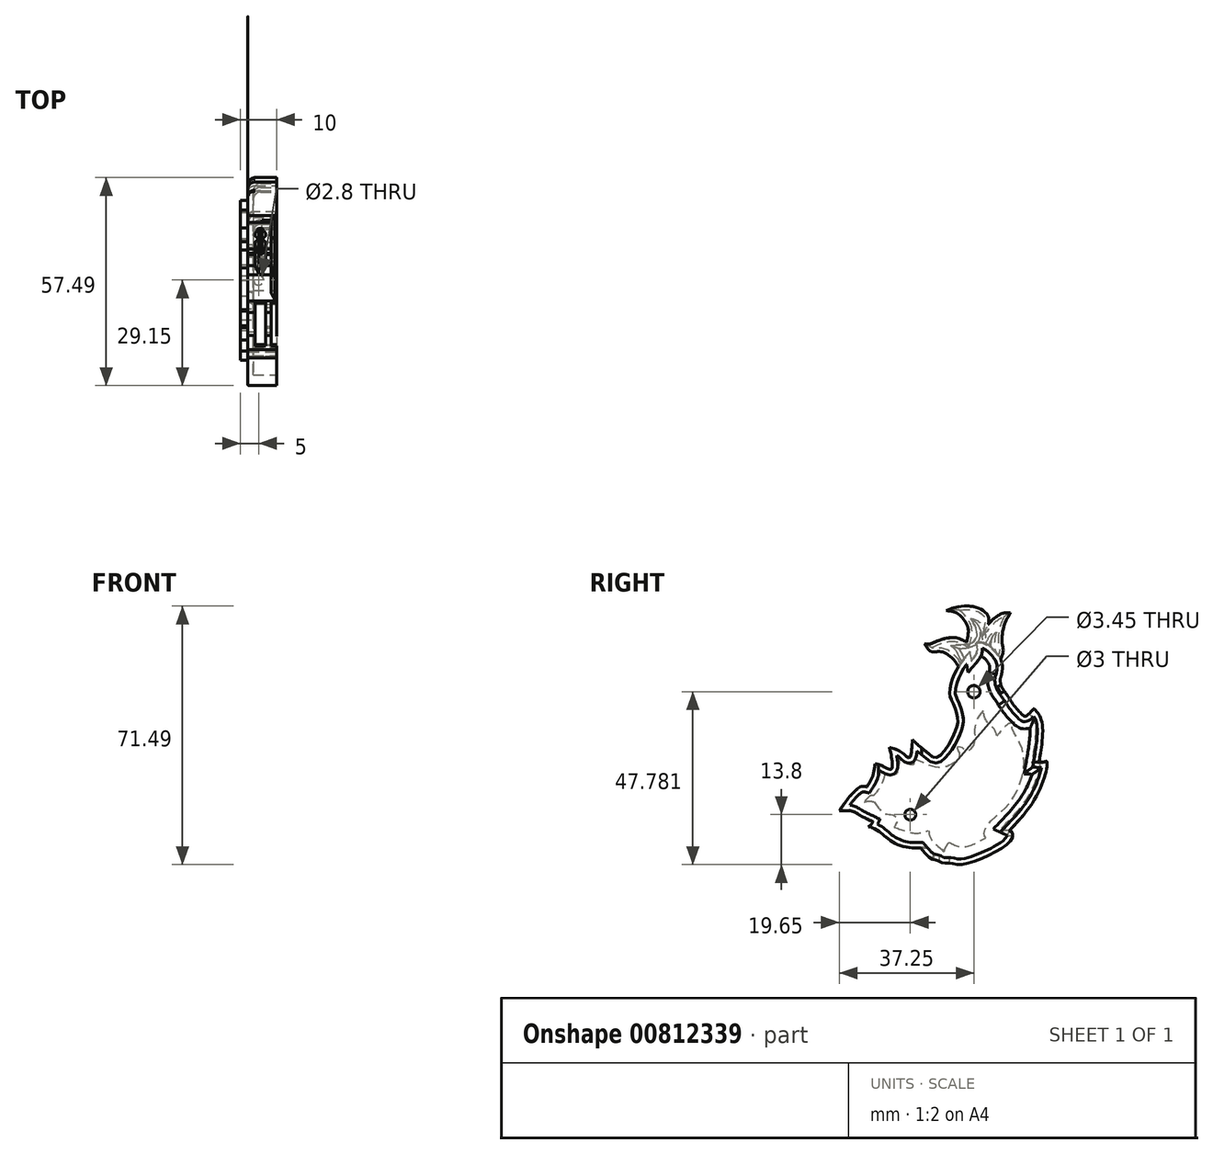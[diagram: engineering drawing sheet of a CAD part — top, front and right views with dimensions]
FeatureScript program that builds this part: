
annotation { "Feature Type Name" : "Feature", "Feature Type Description" : "" }
export const myFeature = defineFeature(function(context is Context, id is Id, definition is map)
    precondition{}
    {
        {
            var Q0;
            Q0=qCreatedBy(makeId("Right.planeOp"),FACE);
            var sketch = newSketch(context, id + "F0", { "sketchPlane" : qUnion([Q0])});
            skPoint(sketch, "E0", {"position": v(40.6, 0) * mm});
            skPoint(sketch, "E1", {"position": v(0, -40.6) * mm});
            skSolve(sketch);
        }
        {
            var Q0;
            Q0=qCreatedBy(makeId("Right.planeOp"),FACE);
            var sketch = newSketch(context, id + "F1", { "sketchPlane" : qUnion([Q0])});
            skFitSpline(sketch, "E2", {"points": [v(-3.24, 0) * mm, v(0.5, -2.14) * mm, v(5.33, 4.74) * mm, v(6.1, 8.94) * mm, v(4.7, 13.13) * mm, v(3.93, 15.55) * mm, v(4.82, 19.88) * mm, v(6.47, 23.19) * mm], "startDerivative": vector(37.62, -30.46) * mm, "endDerivative": vector(13.33, 23.15) * mm});
            skFitSpline(sketch, "E3", {"points": [v(6.47, 23.19) * mm, v(7.57, 24.79) * mm, v(9.54, 27.14) * mm], "startDerivative": vector(2.25, 3.48) * mm, "endDerivative": vector(3.82, 4.4) * mm});
            skFitSpline(sketch, "E4", {"points": [v(9.54, 27.14) * mm, v(9.93, 24.79) * mm], "startDerivative": vector(0.4, -2.35) * mm, "endDerivative": vector(0.4, -2.35) * mm});
            skFitSpline(sketch, "E5", {"points": [v(9.93, 24.79) * mm, v(11.4, 27.14) * mm, v(11.1, 29.4) * mm], "startDerivative": vector(3.7, 4.42) * mm, "endDerivative": vector(-1.43, 4.81) * mm});
            skFitSpline(sketch, "E6", {"points": [v(11.1, 29.4) * mm, v(11.78, 29.7) * mm, v(12.83, 29.7) * mm, v(15.34, 28.3) * mm, v(18.25, 24.34) * mm, v(18.14, 20.25) * mm], "startDerivative": vector(5.83, 3.18) * mm, "endDerivative": vector(-3.05, -15.82) * mm});
            skFitSpline(sketch, "E7", {"points": [v(20.33, 14.28) * mm, v(23.93, 9.7) * mm, v(24.82, 9.24) * mm, v(27.16, 11.36) * mm], "startDerivative": vector(7.36, -13.07) * mm, "endDerivative": vector(7.66, 8.58) * mm});
            skFitSpline(sketch, "E8", {"points": [v(27.16, 11.36) * mm, v(28.52, 9.77) * mm, v(29.58, 6.07) * mm, v(28.98, -1.2) * mm, v(28.6, -3.47) * mm], "startDerivative": vector(7.57, -7.48) * mm, "endDerivative": vector(-1.64, -9.32) * mm});
            skFitSpline(sketch, "E9", {"points": [v(28.6, -3.47) * mm, v(29.59, -3.47) * mm, v(30.76, -3.19) * mm], "startDerivative": vector(2.05, -0.13) * mm, "endDerivative": vector(2.26, 0.67) * mm});
            skFitSpline(sketch, "E10", {"points": [v(30.76, -3.19) * mm, v(30.76, -5.2) * mm, v(27.33, -13.82) * mm, v(20.4, -22.38) * mm], "startDerivative": vector(1.2, -9.04) * mm, "endDerivative": vector(-17.5, -18.45) * mm});
            skFitSpline(sketch, "E11", {"points": [v(20.4, -22.38) * mm, v(21.13, -22.88) * mm, v(21.29, -24.17) * mm, v(19.32, -26.59) * mm, v(12.59, -30.14) * mm, v(6.69, -31.8) * mm, v(4.01, -31.38) * mm, v(2.05, -31.37) * mm, v(0.26, -30.52) * mm, v(-0.96, -30.31) * mm, v(-4.15, -27.22) * mm], "startDerivative": vector(14.78, -6.8) * mm, "endDerivative": vector(-27.99, 32.68) * mm});
            skFitSpline(sketch, "E12", {"points": [v(-4.15, -27.22) * mm, v(-8.6, -26.89) * mm, v(-12.79, -24.96) * mm, v(-15.21, -22.93) * mm, v(-17.91, -21.45) * mm, v(-18.54, -21.31) * mm], "startDerivative": vector(-18.02, -0.18) * mm, "endDerivative": vector(-5.5, 0.56) * mm});
            skFitSpline(sketch, "E13", {"points": [v(-18.54, -21.31) * mm, v(-17.72, -20.58) * mm, v(-17.36, -19.97) * mm], "startDerivative": vector(1.69, 1.29) * mm, "endDerivative": vector(0.63, 1.4) * mm});
            skPoint(sketch, "E14.end.orphan", {"position": v(-24.75, -14.2) * mm});
            skFitSpline(sketch, "E15", {"points": [v(-17.36, -19.97) * mm, v(-21.03, -18.12) * mm, v(-23.14, -17.03) * mm, v(-26.65, -16.95) * mm], "startDerivative": vector(-10.75, 5.04) * mm, "endDerivative": vector(-11.13, -0.75) * mm});
            skFitSpline(sketch, "E16", {"points": [v(-26.65, -16.95) * mm, v(-23.68, -12.9) * mm, v(-20.64, -10.25) * mm, v(-19, -10.33) * mm], "startDerivative": vector(6.9, 10.1) * mm, "endDerivative": vector(6.75, -1.8) * mm});
            skFitSpline(sketch, "E17", {"points": [v(-19, -10.33) * mm, v(-17.46, -7.5) * mm, v(-16.72, -3.96) * mm], "startDerivative": vector(3.61, 5.56) * mm, "endDerivative": vector(0.98, 7.15) * mm});
            skFitSpline(sketch, "E18", {"points": [v(-16.72, -3.96) * mm, v(-14.8, -4.47) * mm, v(-12.27, -5.38) * mm, v(-12.38, -1.03) * mm, v(-12.78, 0.59) * mm], "startDerivative": vector(7.9, -0.88) * mm, "endDerivative": vector(-1.71, 5.84) * mm});
            skFitSpline(sketch, "E19", {"points": [v(-12.78, 0.59) * mm, v(-9.24, -0.83) * mm, v(-7.22, -2.24) * mm, v(-6.43, 2.8) * mm], "startDerivative": vector(10.6, -2.72) * mm, "endDerivative": vector(0.94, 15.88) * mm});
            skFitSpline(sketch, "E20", {"points": [v(-6.43, 2.8) * mm, v(-4.74, 1.17) * mm, v(-3.24, 0) * mm], "startDerivative": vector(3.21, -3.25) * mm, "endDerivative": vector(3.16, -2.33) * mm});
            skFitSpline(sketch, "E21", {"points": [v(20.33, 14.28) * mm, v(19.55, 15.4) * mm, v(18.07, 17.87) * mm, v(18.14, 20.25) * mm], "startDerivative": vector(-3.19, 3.99) * mm, "endDerivative": vector(2.56, 3.4) * mm});
            skSolve(sketch);
        }
        {
            var Q0;
            Q0 = qSketchRegion(id + "F1", true);
            extrude(context, id + "F2", {"entities" : qUnion([Q0]), "oppositeDirection" : true, "depth" : 8 * mm, "offsetDistance" : 25 * mm});
        }
        {
            var Q0;
            Q0=qCreatedBy(makeId("Right.planeOp"),FACE);
            var sketch = newSketch(context, id + "F3", { "sketchPlane" : qUnion([Q0])});
            skCircle(sketch, "E22", {"center": v(10.6, 15.98) * mm, "radius": 1.73 * mm});
            skSolve(sketch);
        }
        {
            var Q0;
            Q0=makeQuery(id+"F2.opExtrude","CAP_FACE",FACE,{"disambiguationData":[OSD([sQuery(id+"F1.wireOp",EDGE,"E2"),sQuery(id+"F1.wireOp",EDGE,"E3"),sQuery(id+"F1.wireOp",EDGE,"E4"),sQuery(id+"F1.wireOp",EDGE,"E5"),sQuery(id+"F1.wireOp",EDGE,"E6"),sQuery(id+"F1.wireOp",EDGE,"b648baaf-3003-42c2-b2da-362ff8d469fc"),sQuery(id+"F1.wireOp",EDGE,"f09f861e-65dd-4840-b0a7-49bf3a0d17f7"),sQuery(id+"F1.wireOp",EDGE,"9c976f9a-3d35-419b-9c2e-039097bb7361"),sQuery(id+"F1.wireOp",EDGE,"E7"),sQuery(id+"F1.wireOp",EDGE,"E8"),sQuery(id+"F1.wireOp",EDGE,"E9"),sQuery(id+"F1.wireOp",EDGE,"E10"),sQuery(id+"F1.wireOp",EDGE,"E11"),sQuery(id+"F1.wireOp",EDGE,"E12"),sQuery(id+"F1.wireOp",EDGE,"E13"),sQuery(id+"F1.wireOp",EDGE,"E15"),sQuery(id+"F1.wireOp",EDGE,"E16"),sQuery(id+"F1.wireOp",EDGE,"E17"),sQuery(id+"F1.wireOp",EDGE,"E18"),sQuery(id+"F1.wireOp",EDGE,"E19"),sQuery(id+"F1.wireOp",EDGE,"E20")])],"isStart":true});
            shell(context, id + "F4", {"entities" : qUnion([Q0]), "thickness" : 1.5 * mm});
        }
        {
            var Q0;
            Q0 = qSketchRegion(id + "F3", true);
            extrude(context, id + "F5", {"entities" : qUnion([Q0]), "operationType" : NewBodyOperationType.REMOVE, "oppositeDirection" : true, "depth" : 25 * mm, "offsetDistance" : 25 * mm});
        }
        {
            var Q0;
            Q0=makeQuery(id+"F2.opExtrude","CAP_FACE",FACE,{"disambiguationData":[OSD([sQuery(id+"F1.wireOp",EDGE,"E2"),sQuery(id+"F1.wireOp",EDGE,"E3"),sQuery(id+"F1.wireOp",EDGE,"E4"),sQuery(id+"F1.wireOp",EDGE,"E5"),sQuery(id+"F1.wireOp",EDGE,"E6"),sQuery(id+"F1.wireOp",EDGE,"b648baaf-3003-42c2-b2da-362ff8d469fc"),sQuery(id+"F1.wireOp",EDGE,"f09f861e-65dd-4840-b0a7-49bf3a0d17f7"),sQuery(id+"F1.wireOp",EDGE,"9c976f9a-3d35-419b-9c2e-039097bb7361"),sQuery(id+"F1.wireOp",EDGE,"E7"),sQuery(id+"F1.wireOp",EDGE,"E8"),sQuery(id+"F1.wireOp",EDGE,"E9"),sQuery(id+"F1.wireOp",EDGE,"E10"),sQuery(id+"F1.wireOp",EDGE,"E11"),sQuery(id+"F1.wireOp",EDGE,"E12"),sQuery(id+"F1.wireOp",EDGE,"E13"),sQuery(id+"F1.wireOp",EDGE,"E15"),sQuery(id+"F1.wireOp",EDGE,"E16"),sQuery(id+"F1.wireOp",EDGE,"E17"),sQuery(id+"F1.wireOp",EDGE,"E18"),sQuery(id+"F1.wireOp",EDGE,"E19"),sQuery(id+"F1.wireOp",EDGE,"E20")])],"isStart":false});
            var sketch = newSketch(context, id + "F6", { "sketchPlane" : qUnion([Q0])});
            skFitSpline(sketch, "E23", {"points": [v(-16.94, 3.72) * mm, v(-16.28, 5.54) * mm, v(-14.13, 7.85) * mm, v(-13.14, 10.82) * mm], "startDerivative": vector(1.3, 6.56) * mm, "endDerivative": vector(1.63, 8.78) * mm});
            skFitSpline(sketch, "E24", {"points": [v(-13.14, 10.82) * mm, v(-11, 7.19) * mm, v(-10.83, 3.06) * mm, v(-10.34, 1.08) * mm, v(-8.63, -0.5) * mm, v(-7.42, 0.48) * mm, v(-5.9, 0.63) * mm], "startDerivative": vector(12.48, -15.59) * mm, "endDerivative": vector(12.54, -1.6) * mm});
            skFitSpline(sketch, "E25", {"points": [v(-5.9, 0.63) * mm, v(-6.36, -0.5) * mm, v(-6.5, -2.1) * mm, v(-4.54, -3.99) * mm, v(-0.91, -4.97) * mm, v(5.75, -2.55) * mm], "startDerivative": vector(-3.58, -8.34) * mm, "endDerivative": vector(23, 11.15) * mm});
            skFitSpline(sketch, "E26", {"points": [v(5.75, -2.55) * mm, v(6.02, -3.35) * mm, v(5.94, -4.12) * mm], "startDerivative": vector(0.72, -1.57) * mm, "endDerivative": vector(-0.34, -1.59) * mm});
            skFitSpline(sketch, "E27", {"points": [v(5.94, -4.12) * mm, v(7.2, -4.12) * mm, v(9.02, -2.97) * mm, v(10.18, -1.51) * mm], "startDerivative": vector(4.26, -0.66) * mm, "endDerivative": vector(2.95, 4.28) * mm});
            skFitSpline(sketch, "E28", {"points": [v(10.18, -1.51) * mm, v(10.03, -3.22) * mm, v(10.7, -6.67) * mm], "startDerivative": vector(-0.7, -3.8) * mm, "endDerivative": vector(1.58, -6.36) * mm});
            skFitSpline(sketch, "E29", {"points": [v(10.7, -6.67) * mm, v(11.92, -7.06) * mm, v(14.12, -6.34) * mm], "startDerivative": vector(2.66, -1.38) * mm, "endDerivative": vector(4.12, 1.88) * mm});
            skFitSpline(sketch, "E30", {"points": [v(14.12, -6.34) * mm, v(14.57, -8.77) * mm, v(16.73, -12.28) * mm, v(17.18, -12.77) * mm], "startDerivative": vector(0.23, -6.2) * mm, "endDerivative": vector(1.91, -1.84) * mm});
            skFitSpline(sketch, "E31", {"points": [v(17.18, -12.77) * mm, v(18, -12.77) * mm, v(19.7, -14.48) * mm], "startDerivative": vector(2.13, 0.5) * mm, "endDerivative": vector(2.86, -3.54) * mm});
            skFitSpline(sketch, "E32", {"points": [v(19.7, -14.48) * mm, v(18.4, -14.25) * mm, v(16.95, -14.48) * mm], "startDerivative": vector(-2.64, 0.68) * mm, "endDerivative": vector(-2.86, -0.67) * mm});
            skFitSpline(sketch, "E33", {"points": [v(16.95, -14.48) * mm, v(15.69, -16.27) * mm, v(14.12, -17.67) * mm, v(11.9, -18.08) * mm, v(10.7, -19.01) * mm, v(10.9, -20.53) * mm, v(11.43, -21.46) * mm], "startDerivative": vector(-6.56, -9.7) * mm, "endDerivative": vector(4.17, -6.37) * mm});
            skFitSpline(sketch, "E34", {"points": [v(11.43, -21.46) * mm, v(7.7, -22.72) * mm, v(4.92, -23.12) * mm, v(1.9, -22.38) * mm], "startDerivative": vector(-10.55, -3.79) * mm, "endDerivative": vector(-9.42, 3.13) * mm});
            skFitSpline(sketch, "E35", {"points": [v(1.9, -22.38) * mm, v(1.33, -24.66) * mm, v(-2.36, -28.17) * mm], "startDerivative": vector(-0.45, -5.6) * mm, "endDerivative": vector(-7.62, -5.97) * mm});
            skFitSpline(sketch, "E36", {"points": [v(-2.36, -28.17) * mm, v(-2.8, -27) * mm, v(-3.7, -25.65) * mm], "startDerivative": vector(-0.8, 2.5) * mm, "endDerivative": vector(-1.88, 2.55) * mm});
            skFitSpline(sketch, "E37", {"points": [v(-3.7, -25.65) * mm, v(-6.46, -26.79) * mm, v(-9.3, -26.6) * mm, v(-13.93, -24.36) * mm], "startDerivative": vector(-9.04, -4.62) * mm, "endDerivative": vector(-12.18, 6.83) * mm});
            skFitSpline(sketch, "E38", {"points": [v(-13.93, -24.36) * mm, v(-13.5, -23.75) * mm, v(-13.5, -22.38) * mm, v(-15.76, -19.24) * mm, v(-19.88, -15.51) * mm, v(-23.5, -8.94) * mm, v(-24.41, -2.03) * mm, v(-22.5, 3.31) * mm, v(-21.1, 6.11) * mm, v(-21.87, 7.51) * mm], "startDerivative": vector(9.7, 10.6) * mm, "endDerivative": vector(-15.5, 17.7) * mm});
            skFitSpline(sketch, "E39", {"points": [v(-21.87, 7.51) * mm, v(-20.07, 7.05) * mm, v(-16.94, 3.72) * mm], "startDerivative": vector(4.52, -0.37) * mm, "endDerivative": vector(5.28, -6.74) * mm});
            skSolve(sketch);
        }
        {
            var Q0;
            Q0 = qSketchRegion(id + "F6", true);
            extrude(context, id + "F7", {"entities" : qUnion([Q0]), "operationType" : NewBodyOperationType.ADD, "depth" : 2 * mm, "offsetDistance" : 25 * mm});
        }
        {
            var Q0;
            Q0=qCreatedBy(makeId("Right.planeOp"),FACE);
            var sketch = newSketch(context, id + "F8", { "sketchPlane" : qUnion([Q0])});
            skCircle(sketch, "E40", {"center": v(-7, -18) * mm, "radius": 1.5 * mm});
            skSolve(sketch);
        }
        {
            var Q0;
            Q0 = qSketchRegion(id + "F8", true);
            extrude(context, id + "F9", {"entities" : qUnion([Q0]), "operationType" : NewBodyOperationType.REMOVE, "oppositeDirection" : true, "depth" : 25 * mm, "offsetDistance" : 25 * mm});
        }
        {
            var Q0;
            Q0=qCreatedBy(makeId("Top.planeOp"),FACE);
            var sketch = newSketch(context, id + "F10", { "sketchPlane" : qUnion([Q0])});
            skLineSegment(sketch, "E41.bottom", {"start": v(-1.5, -3.8) * mm, "end": v(1.5, -3.8) * mm});
            skLineSegment(sketch, "E41.top", {"start": v(-1.5, -15.8) * mm, "end": v(1.5, -15.8) * mm});
            skLineSegment(sketch, "E41.left", {"start": v(-1.5, -3.8) * mm, "end": v(-1.5, -15.8) * mm});
            skLineSegment(sketch, "E41.right", {"start": v(1.5, -3.8) * mm, "end": v(1.5, -15.8) * mm});
            skPoint(sketch, "E42", {"position": v(0, -3.8) * mm});
            skLineSegment(sketch, "E43.1.0.0", {"start": v(-6, -3.8) * mm, "end": v(-6, -15.8) * mm});
            skLineSegment(sketch, "E43.1.0.1", {"start": v(-3, -3.8) * mm, "end": v(-3, -15.8) * mm});
            skLineSegment(sketch, "E43.1.0.2", {"start": v(-6, -3.8) * mm, "end": v(-3, -3.8) * mm});
            skLineSegment(sketch, "E43.1.0.3", {"start": v(-6, -15.8) * mm, "end": v(-3, -15.8) * mm});
            skLineSegment(sketch, "E43.direction1", {"start": v(-1.6, -18.6) * mm, "end": v(-6.1, -18.6) * mm, "construction": true});
            skSolve(sketch);
        }
        {
            var Q0;
            Q0 = qSketchRegion(id + "F10", true);
            extrude(context, id + "F11", {"entities" : qUnion([Q0]), "operationType" : NewBodyOperationType.REMOVE, "depth" : 25 * mm, "offsetDistance" : 25 * mm, "symmetric" : true});
        }
        {
            var Q0;
            Q0=qCreatedBy(makeId("Right.planeOp"),FACE);
            var sketch = newSketch(context, id + "F12", { "sketchPlane" : qUnion([Q0])});
            skFitSpline(sketch, "E44", {"points": [v(17.69, 24.4) * mm, v(18.68, 27.2) * mm, v(18.35, 29.84) * mm, v(19, 34.45) * mm, v(20.66, 37.75) * mm], "startDerivative": vector(6.01, 12.4) * mm, "endDerivative": vector(7.04, 11.68) * mm});
            skFitSpline(sketch, "E45", {"points": [v(20.66, 37.75) * mm, v(18.84, 37.75) * mm, v(16.37, 36.43) * mm, v(14.55, 34.62) * mm], "startDerivative": vector(-5.99, 0.78) * mm, "endDerivative": vector(-4.77, -5.4) * mm});
            skFitSpline(sketch, "E46", {"points": [v(14.55, 34.62) * mm, v(14.55, 36.76) * mm, v(11.58, 39.24) * mm, v(5.8, 39.4) * mm, v(3, 38.41) * mm], "startDerivative": vector(2.15, 11) * mm, "endDerivative": vector(-10.72, -4.87) * mm});
            skFitSpline(sketch, "E47", {"points": [v(3, 38.41) * mm, v(5.52, 37.92) * mm, v(7.73, 36) * mm, v(9.02, 33.25) * mm, v(8.55, 29.7) * mm], "startDerivative": vector(11.26, -0.86) * mm, "endDerivative": vector(-3.36, -13.51) * mm});
            skFitSpline(sketch, "E48", {"points": [v(8.55, 29.7) * mm, v(7.02, 30.48) * mm, v(4.76, 30.97) * mm, v(0.64, 30.09) * mm, v(-1.62, 29.2) * mm, v(-3.09, 29.3) * mm], "startDerivative": vector(-8.64, 4.8) * mm, "endDerivative": vector(-9.14, 1.75) * mm});
            skFitSpline(sketch, "E49", {"points": [v(-3.09, 29.3) * mm, v(-2.24, 28.07) * mm, v(-1.26, 27.1) * mm, v(0.6, 27.1) * mm, v(2.66, 26.7) * mm, v(5.21, 24.64) * mm, v(6.49, 22.58) * mm], "startDerivative": vector(5.9, -8.55) * mm, "endDerivative": vector(5.75, -11.3) * mm});
            skLineSegment(sketch, "E50", {"start": v(6.49, 22.58) * mm, "end": v(9.04, 25.33) * mm});
            skLineSegment(sketch, "E51", {"start": v(9.04, 25.33) * mm, "end": v(9.43, 23.17) * mm});
            skLineSegment(sketch, "E52", {"start": v(9.43, 23.17) * mm, "end": v(12.18, 26.4) * mm});
            skLineSegment(sketch, "E53", {"start": v(12.18, 26.4) * mm, "end": v(12.18, 28.76) * mm});
            skLineSegment(sketch, "E54", {"start": v(12.18, 28.76) * mm, "end": v(13.45, 28.76) * mm});
            skLineSegment(sketch, "E55", {"start": v(13.45, 28.76) * mm, "end": v(15.9, 26.7) * mm});
            skLineSegment(sketch, "E56", {"start": v(15.9, 26.7) * mm, "end": v(17.69, 24.4) * mm});
            skSolve(sketch);
        }
        {
            var Q0;
            Q0 = qSketchRegion(id + "F12", true);
            extrude(context, id + "F13", {"entities" : qUnion([Q0]), "operationType" : NewBodyOperationType.ADD, "oppositeDirection" : true, "depth" : 1.5 * mm, "offsetDistance" : 25 * mm});
        }
        {
            var Q0;
            Q0=qCreatedBy(makeId("Right.planeOp"),FACE);
            cPlane(context, id + "F14", {"entities" : qUnion([Q0]), "cplaneType" : CPlaneType.OFFSET, "offset" : 3 * mm, "oppositeDirection" : true, "width" : 150 * mm, "height" : 150 * mm});
        }
        {
            var Q0;
            Q0=qCreatedBy(id+"F14.planeOp",FACE);
            var sketch = newSketch(context, id + "F15", { "sketchPlane" : qUnion([Q0])});
            skFitSpline(sketch, "E57", {"points": [v(17.1, 25.96) * mm, v(16.88, 26.64) * mm, v(16.3, 28.17) * mm, v(16.8, 32.5) * mm], "startDerivative": vector(1.16, 6.3) * mm, "endDerivative": vector(2.86, 11.3) * mm});
            skFitSpline(sketch, "E58", {"points": [v(16.8, 32.5) * mm, v(15.5, 32) * mm, v(13.98, 29.58) * mm], "startDerivative": vector(-3.3, -0.62) * mm, "endDerivative": vector(-2.39, -4.95) * mm});
            skFitSpline(sketch, "E59", {"points": [v(13.98, 29.58) * mm, v(13.76, 31.55) * mm, v(12.98, 34.13) * mm, v(11.37, 35.8) * mm, v(9.66, 36.25) * mm], "startDerivative": vector(-0.65, 7.9) * mm, "endDerivative": vector(-7.71, 1.15) * mm});
            skFitSpline(sketch, "E60", {"points": [v(9.66, 36.25) * mm, v(10.54, 34.83) * mm, v(11.41, 32.5) * mm, v(10.63, 29.94) * mm, v(8.28, 29.06) * mm, v(4.13, 28.83) * mm], "startDerivative": vector(5.33, -8.41) * mm, "endDerivative": vector(-17.42, -0.5) * mm});
            skFitSpline(sketch, "E61", {"points": [v(4.13, 28.83) * mm, v(5.46, 27.54) * mm, v(7.26, 24.27) * mm], "startDerivative": vector(3.27, -2.61) * mm, "endDerivative": vector(3.02, -6.3) * mm});
            skLineSegment(sketch, "E62", {"start": v(7.26, 24.27) * mm, "end": v(8.55, 25.47) * mm});
            skLineSegment(sketch, "E63", {"start": v(8.55, 25.47) * mm, "end": v(8.97, 23.25) * mm});
            skLineSegment(sketch, "E64", {"start": v(8.97, 23.25) * mm, "end": v(11.69, 26.48) * mm});
            skLineSegment(sketch, "E65", {"start": v(11.69, 26.48) * mm, "end": v(12.29, 29.66) * mm});
            skLineSegment(sketch, "E66", {"start": v(12.29, 29.66) * mm, "end": v(13.3, 29.15) * mm});
            skLineSegment(sketch, "E67", {"start": v(13.3, 29.15) * mm, "end": v(15.15, 27.96) * mm});
            skLineSegment(sketch, "E68", {"start": v(15.15, 27.96) * mm, "end": v(16.85, 25.47) * mm});
            skLineSegment(sketch, "E69", {"start": v(16.85, 25.47) * mm, "end": v(17.1, 25.96) * mm});
            skSolve(sketch);
        }
        {
            var Q0;
            Q0 = qSketchRegion(id + "F15", true);
            extrude(context, id + "F16", {"entities" : qUnion([Q0]), "operationType" : NewBodyOperationType.ADD, "oppositeDirection" : true, "depth" : 3 * mm, "offsetDistance" : 25 * mm});
        }
        {
            var Q0;
            Q0=qCreatedBy(makeId("Top.planeOp"),FACE);
            cPlane(context, id + "F17", {"entities" : qUnion([Q0]), "cplaneType" : CPlaneType.OFFSET, "offset" : 28 * mm, "oppositeDirection" : true, "width" : 150 * mm, "height" : 150 * mm});
        }
        {
            var Q0;
            Q0=qCreatedBy(id+"F17.planeOp",FACE);
            var sketch = newSketch(context, id + "F18", { "sketchPlane" : qUnion([Q0])});
            skCircle(sketch, "E70", {"center": v(-5, 2.5) * mm, "radius": 1.4 * mm});
            skSolve(sketch);
        }
        {
            var Q0;
            Q0 = qSketchRegion(id + "F18", true);
            extrude(context, id + "F19", {"entities" : qUnion([Q0]), "operationType" : NewBodyOperationType.REMOVE, "oppositeDirection" : true, "depth" : 5 * mm, "offsetDistance" : 25 * mm});
        }
        {
            var Q0;
            Q0=makeQuery(id+"F13.opExtrude","CAP_EDGE",EDGE,{"disambiguationData":[OSD([sQuery(id+"F12.wireOp",EDGE,"E46")])],"isStart":false});
            var Q1;
            Q1=makeQuery(id+"F13.opExtrude","CAP_EDGE",EDGE,{"disambiguationData":[OSD([sQuery(id+"F12.wireOp",EDGE,"E45")])],"isStart":false});
            var Q2;
            Q2=makeQuery(id+"F13.opExtrude","CAP_EDGE",EDGE,{"disambiguationData":[OSD([sQuery(id+"F12.wireOp",EDGE,"E44")])],"isStart":false});
            var Q3;
            Q3=makeQuery(id+"F13.opExtrude","CAP_EDGE",EDGE,{"disambiguationData":[OSD([sQuery(id+"F12.wireOp",EDGE,"E47")])],"isStart":false});
            var Q4;
            Q4=makeQuery(id+"F13.opExtrude","CAP_EDGE",EDGE,{"disambiguationData":[OSD([sQuery(id+"F12.wireOp",EDGE,"E48")])],"isStart":false});
            var Q5;
            Q5=makeQuery(id+"F13.opExtrude","CAP_EDGE",EDGE,{"disambiguationData":[OSD([sQuery(id+"F12.wireOp",EDGE,"E49")])],"isStart":false});
            chamfer(context, id + "F20", {"entities" : qUnion([Q0, Q1, Q2, Q3, Q4, Q5]), "width" : 1 * mm, "tangentPropagation" : true});
        }
        {
            var Q0;
            Q0=makeQuery(id+"F16.opExtrude","CAP_EDGE",EDGE,{"disambiguationData":[OSD([sQuery(id+"F15.wireOp",EDGE,"E59")])],"isStart":false});
            var Q1;
            Q1=makeQuery(id+"F16.opExtrude","CAP_EDGE",EDGE,{"disambiguationData":[OSD([sQuery(id+"F15.wireOp",EDGE,"E59")])],"isStart":true});
            var Q2;
            Q2=makeQuery(id+"F16.opExtrude","CAP_EDGE",EDGE,{"disambiguationData":[OSD([sQuery(id+"F15.wireOp",EDGE,"E58")])],"isStart":false});
            var Q3;
            Q3=makeQuery(id+"F16.opExtrude","CAP_EDGE",EDGE,{"disambiguationData":[OSD([sQuery(id+"F15.wireOp",EDGE,"E58")])],"isStart":true});
            var Q4;
            Q4=makeQuery(id+"F16.opExtrude","CAP_EDGE",EDGE,{"disambiguationData":[OSD([sQuery(id+"F15.wireOp",EDGE,"E57")])],"isStart":false});
            var Q5;
            Q5=makeQuery(id+"F16.opExtrude","CAP_EDGE",EDGE,{"disambiguationData":[OSD([sQuery(id+"F15.wireOp",EDGE,"E57")])],"isStart":true});
            var Q6;
            Q6=makeQuery(id+"F16.opExtrude","CAP_EDGE",EDGE,{"disambiguationData":[OSD([sQuery(id+"F15.wireOp",EDGE,"E60")])],"isStart":true});
            var Q7;
            Q7=makeQuery(id+"F16.opExtrude","CAP_EDGE",EDGE,{"disambiguationData":[OSD([sQuery(id+"F15.wireOp",EDGE,"E60")])],"isStart":false});
            var Q8;
            Q8=makeQuery(id+"F16.opExtrude","CAP_EDGE",EDGE,{"disambiguationData":[OSD([sQuery(id+"F15.wireOp",EDGE,"E61")])],"isStart":false});
            var Q9;
            Q9=makeQuery(id+"F16.opExtrude","CAP_EDGE",EDGE,{"disambiguationData":[OSD([sQuery(id+"F15.wireOp",EDGE,"E61")])],"isStart":true});
            chamfer(context, id + "F21", {"entities" : qUnion([Q0, Q1, Q2, Q3, Q4, Q5, Q6, Q7, Q8, Q9]), "width" : 1 * mm, "tangentPropagation" : true});
        }
        {
            var Q0;
            Q0=qCreatedBy(makeId("Right.planeOp"),FACE);
            var sketch = newSketch(context, id + "F22", { "sketchPlane" : qUnion([Q0])});
            skLineSegment(sketch, "E71", {"start": v(17.04, 17.32) * mm, "end": v(18.36, 18.03) * mm});
            skLineSegment(sketch, "E72", {"start": v(18.36, 18.03) * mm, "end": v(19.3, 16.26) * mm});
            skLineSegment(sketch, "E73", {"start": v(19.3, 16.26) * mm, "end": v(17.98, 15.56) * mm});
            skLineSegment(sketch, "E74", {"start": v(17.04, 17.32) * mm, "end": v(17.98, 15.56) * mm});
            skSolve(sketch);
        }
        {
            var Q0;
            Q0 = qSketchRegion(id + "F22", true);
            extrude(context, id + "F23", {"entities" : qUnion([Q0]), "operationType" : NewBodyOperationType.REMOVE, "oppositeDirection" : true, "depth" : 4 * mm, "offsetDistance" : 25 * mm});
        }
        {
            var Q0;
            {var subQ0=sQuery(id+"F1.wireOp",EDGE,"E8");Q0=makeQuery(id+"F4.opShell","OFFSET_EDGE",EDGE,{"disambiguationData":[OSD([subQ0]),TDD([makeQuery(id+"F2.opExtrude","CAP_EDGE",EDGE,{"disambiguationData":[OSD([subQ0])],"isStart":false})])]});}
            var Q1;
            {var subQ0=sQuery(id+"F1.wireOp",EDGE,"E10");Q1=makeQuery(id+"F4.opShell","OFFSET_EDGE",EDGE,{"disambiguationData":[OSD([subQ0]),TDD([makeQuery(id+"F2.opExtrude","CAP_EDGE",EDGE,{"disambiguationData":[OSD([subQ0])],"isStart":false})])]});}
            var Q2;
            {var subQ0=sQuery(id+"F1.wireOp",EDGE,"E9");Q2=makeQuery(id+"F4.opShell","OFFSET_EDGE",EDGE,{"disambiguationData":[OSD([subQ0]),TDD([makeQuery(id+"F2.opExtrude","CAP_EDGE",EDGE,{"disambiguationData":[OSD([subQ0])],"isStart":false})])]});}
            var Q3;
            {var subQ0=sQuery(id+"F1.wireOp",EDGE,"E7");Q3=makeQuery(id+"F4.opShell","OFFSET_EDGE",EDGE,{"disambiguationData":[OSD([subQ0]),TDD([makeQuery(id+"F2.opExtrude","CAP_EDGE",EDGE,{"disambiguationData":[OSD([subQ0])],"isStart":false})])]});}
            var Q4;
            {var subQ0=sQuery(id+"F1.wireOp",EDGE,"E21");Q4=makeQuery(id+"F4.opShell","OFFSET_EDGE",EDGE,{"disambiguationData":[OSD([subQ0]),TDD([makeQuery(id+"F2.opExtrude","CAP_EDGE",EDGE,{"disambiguationData":[OSD([subQ0])],"isStart":false})])]});}
            var Q5;
            {var subQ0=sQuery(id+"F1.wireOp",EDGE,"E6");Q5=makeQuery(id+"F4.opShell","OFFSET_EDGE",EDGE,{"disambiguationData":[OSD([subQ0]),TDD([makeQuery(id+"F2.opExtrude","CAP_EDGE",EDGE,{"disambiguationData":[OSD([subQ0])],"isStart":false})])]});}
            fillet(context, id + "F24", {"entities" : qUnion([Q0, Q1, Q2, Q3, Q4, Q5]), "radius" : 2 * mm, "tangentPropagation" : true, "allowEdgeOverflow" : false});
        }
        {
            var Q0;
            Q0=makeQuery(id+"F2.opExtrude","CAP_EDGE",EDGE,{"disambiguationData":[OSD([sQuery(id+"F1.wireOp",EDGE,"E8")])],"isStart":false});
            var Q1;
            Q1=makeQuery(id+"F2.opExtrude","CAP_EDGE",EDGE,{"disambiguationData":[OSD([sQuery(id+"F1.wireOp",EDGE,"E10")])],"isStart":false});
            fillet(context, id + "F25", {"entities" : qUnion([Q0, Q1]), "radius" : 2 * mm, "tangentPropagation" : true, "allowEdgeOverflow" : false});
        }
        {
            var Q0;
            Q0=makeQuery(id+"F2.opExtrude","CAP_EDGE",EDGE,{"disambiguationData":[OSD([sQuery(id+"F1.wireOp",EDGE,"E6")])],"isStart":false});
            var Q1;
            Q1=makeQuery(id+"F2.opExtrude","CAP_EDGE",EDGE,{"disambiguationData":[OSD([sQuery(id+"F1.wireOp",EDGE,"E21")])],"isStart":false});
            var Q2;
            Q2=makeQuery(id+"F2.opExtrude","CAP_EDGE",EDGE,{"disambiguationData":[OSD([sQuery(id+"F1.wireOp",EDGE,"E7")])],"isStart":false});
            var Q3;
            Q3=makeQuery(id+"F2.opExtrude","CAP_EDGE",EDGE,{"disambiguationData":[OSD([sQuery(id+"F1.wireOp",EDGE,"E5")])],"isStart":false});
            var Q4;
            Q4=makeQuery(id+"F2.opExtrude","CAP_EDGE",EDGE,{"disambiguationData":[OSD([sQuery(id+"F1.wireOp",EDGE,"E4")])],"isStart":false});
            var Q5;
            Q5=makeQuery(id+"F2.opExtrude","CAP_EDGE",EDGE,{"disambiguationData":[OSD([sQuery(id+"F1.wireOp",EDGE,"E3")])],"isStart":false});
            var Q6;
            Q6=makeQuery(id+"F2.opExtrude","CAP_EDGE",EDGE,{"disambiguationData":[OSD([sQuery(id+"F1.wireOp",EDGE,"E2")])],"isStart":false});
            var Q7;
            Q7=makeQuery(id+"F2.opExtrude","CAP_EDGE",EDGE,{"disambiguationData":[OSD([sQuery(id+"F1.wireOp",EDGE,"E9")])],"isStart":false});
            var Q8;
            Q8=makeQuery(id+"F2.opExtrude","CAP_EDGE",EDGE,{"disambiguationData":[OSD([sQuery(id+"F1.wireOp",EDGE,"E12")])],"isStart":false});
            var Q9;
            Q9=makeQuery(id+"F2.opExtrude","CAP_EDGE",EDGE,{"disambiguationData":[OSD([sQuery(id+"F1.wireOp",EDGE,"E13")])],"isStart":false});
            var Q10;
            Q10=makeQuery(id+"F2.opExtrude","CAP_EDGE",EDGE,{"disambiguationData":[OSD([sQuery(id+"F1.wireOp",EDGE,"E15")])],"isStart":false});
            var Q11;
            Q11=makeQuery(id+"F2.opExtrude","CAP_EDGE",EDGE,{"disambiguationData":[OSD([sQuery(id+"F1.wireOp",EDGE,"E16")])],"isStart":false});
            var Q12;
            Q12=makeQuery(id+"F2.opExtrude","CAP_EDGE",EDGE,{"disambiguationData":[OSD([sQuery(id+"F1.wireOp",EDGE,"E17")])],"isStart":false});
            var Q13;
            Q13=makeQuery(id+"F2.opExtrude","CAP_EDGE",EDGE,{"disambiguationData":[OSD([sQuery(id+"F1.wireOp",EDGE,"E19")])],"isStart":false});
            var Q14;
            Q14=makeQuery(id+"F2.opExtrude","CAP_EDGE",EDGE,{"disambiguationData":[OSD([sQuery(id+"F1.wireOp",EDGE,"E18")])],"isStart":false});
            var Q15;
            Q15=makeQuery(id+"F2.opExtrude","CAP_EDGE",EDGE,{"disambiguationData":[OSD([sQuery(id+"F1.wireOp",EDGE,"E20")])],"isStart":false});
            fillet(context, id + "F26", {"entities" : qUnion([Q0, Q1, Q2, Q3, Q4, Q5, Q6, Q7, Q8, Q9, Q10, Q11, Q12, Q13, Q14, Q15]), "radius" : .2 * mm, "tangentPropagation" : true, "allowEdgeOverflow" : false});
        }
        {
            var Q0;
            Q0=makeQuery(id+"F2.opExtrude","CAP_EDGE",EDGE,{"disambiguationData":[OSD([sQuery(id+"F1.wireOp",EDGE,"E11")])],"isStart":false});
            fillet(context, id + "F27", {"entities" : qUnion([Q0]), "radius" : 1.5 * mm, "tangentPropagation" : true, "allowEdgeOverflow" : false});
        }
    });
